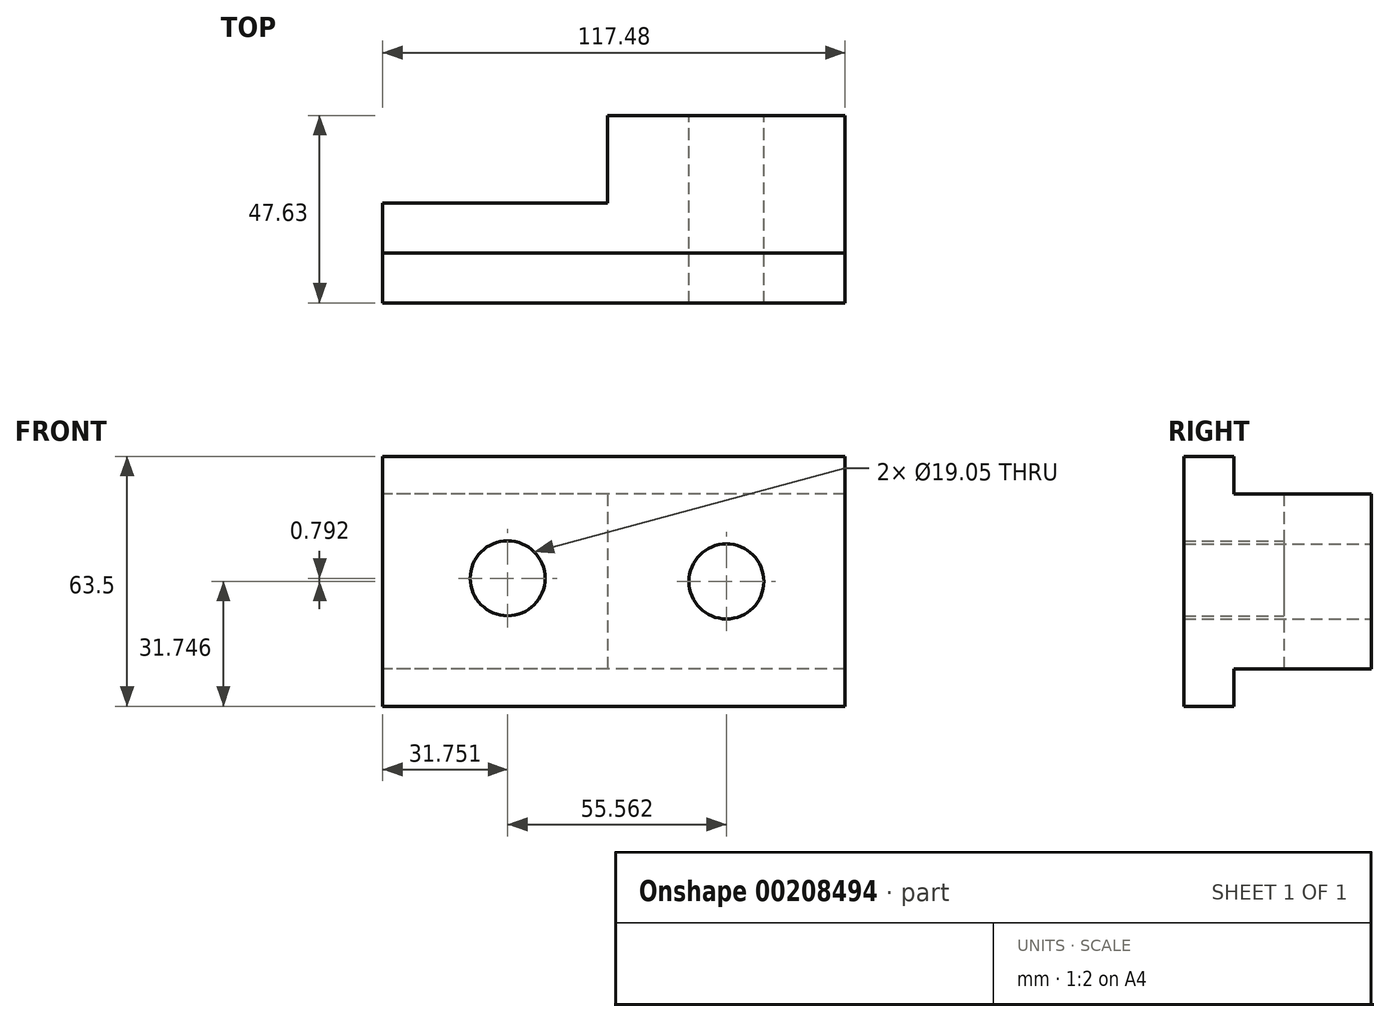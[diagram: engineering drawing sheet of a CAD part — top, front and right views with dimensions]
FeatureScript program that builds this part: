
annotation { "Feature Type Name" : "Feature", "Feature Type Description" : "" }
export const myFeature = defineFeature(function(context is Context, id is Id, definition is map)
    precondition{}
    {
        {
            var Q0;
            Q0=qCreatedBy(makeId("Front.planeOp"),FACE);
            var sketch = newSketch(context, id + "F0", { "sketchPlane" : qUnion([Q0])});
            skLineSegment(sketch, "E0.bottom", {"start": v(30.62, 63.5) * mm, "end": v(148.1, 63.5) * mm});
            skLineSegment(sketch, "E0.top", {"start": v(30.62, 0) * mm, "end": v(148.1, 0) * mm});
            skLineSegment(sketch, "E0.left", {"start": v(30.62, 63.5) * mm, "end": v(30.62, 0) * mm});
            skLineSegment(sketch, "E0.right", {"start": v(148.1, 63.5) * mm, "end": v(148.1, 0) * mm});
            skSolve(sketch);
        }
        {
            var Q0;
            Q0 = qSketchRegion(id + "F0", true);
            extrude(context, id + "F1", {"entities" : qUnion([Q0]), "depth" : 12.7 * mm});
        }
        {
            var Q0;
            Q0=makeQuery(id+"F1.opExtrude","CAP_FACE",FACE,{"disambiguationData":[OSD([sQuery(id+"F0.wireOp",EDGE,"E0.bottom"),sQuery(id+"F0.wireOp",EDGE,"E0.top"),sQuery(id+"F0.wireOp",EDGE,"E0.left"),sQuery(id+"F0.wireOp",EDGE,"E0.right")])],"isStart":true});
            var sketch = newSketch(context, id + "F2", { "sketchPlane" : qUnion([Q0])});
            skLineSegment(sketch, "E1.bottom", {"start": v(-148.1, 53.98) * mm, "end": v(-30.62, 53.98) * mm});
            skLineSegment(sketch, "E1.top", {"start": v(-148.1, 9.53) * mm, "end": v(-30.62, 9.53) * mm});
            skLineSegment(sketch, "E1.left", {"start": v(-148.1, 53.98) * mm, "end": v(-148.1, 9.53) * mm});
            skLineSegment(sketch, "E1.right", {"start": v(-30.62, 53.98) * mm, "end": v(-30.62, 9.53) * mm});
            skSolve(sketch);
        }
        {
            var Q0;
            Q0=makeQuery(id+"F2.imprint","IMPRINT",FACE,{"disambiguationData":[TD([[makeQuery(id+"F2.imprint","IMPRINT",EDGE,{"derivedFrom":sQuery(id+"F2.wireOp",EDGE,"E1.bottom")}),-1.0]])]});
            extrude(context, id + "F3", {"entities" : qUnion([Q0]), "operationType" : NewBodyOperationType.ADD, "depth" : 12.7 * mm});
        }
        {
            var Q0;
            Q0=makeQuery(id+"F3.opExtrude","CAP_FACE",FACE,{"disambiguationData":[OSD([sQuery(id+"F2.wireOp",EDGE,"E1.bottom"),sQuery(id+"F2.wireOp",EDGE,"E1.top"),sQuery(id+"F2.wireOp",EDGE,"E1.left"),sQuery(id+"F2.wireOp",EDGE,"E1.right")])],"isStart":false});
            var sketch = newSketch(context, id + "F4", { "sketchPlane" : qUnion([Q0])});
            skLineSegment(sketch, "E2.bottom", {"start": v(-148.1, 53.98) * mm, "end": v(-87.77, 53.98) * mm});
            skLineSegment(sketch, "E2.top", {"start": v(-148.1, 9.53) * mm, "end": v(-87.77, 9.53) * mm});
            skLineSegment(sketch, "E2.left", {"start": v(-148.1, 53.98) * mm, "end": v(-148.1, 9.53) * mm});
            skLineSegment(sketch, "E2.right", {"start": v(-87.77, 53.98) * mm, "end": v(-87.77, 9.53) * mm});
            skSolve(sketch);
        }
        {
            var Q0;
            Q0 = qSketchRegion(id + "F4", true);
            extrude(context, id + "F5", {"entities" : qUnion([Q0]), "operationType" : NewBodyOperationType.ADD, "depth" : 22.22 * mm});
        }
        {
            var Q0;
            Q0=makeQuery(id+"F3.opExtrude","CAP_FACE",FACE,{"disambiguationData":[OSD([sQuery(id+"F2.wireOp",EDGE,"E1.bottom"),sQuery(id+"F2.wireOp",EDGE,"E1.top"),sQuery(id+"F2.wireOp",EDGE,"E1.left"),sQuery(id+"F2.wireOp",EDGE,"E1.right")])],"isStart":false});
            var sketch = newSketch(context, id + "F6", { "sketchPlane" : qUnion([Q0])});
            skCircle(sketch, "E3", {"center": v(-62.37, 32.55) * mm, "radius": 9.53 * mm});
            skCircle(sketch, "E4", {"center": v(-117.93, 31.76) * mm, "radius": 9.53 * mm});
            skSolve(sketch);
        }
        {
            var Q0;
            Q0 = qSketchRegion(id + "F6", true);
            extrude(context, id + "F7", {"entities" : qUnion([Q0]), "operationType" : NewBodyOperationType.REMOVE, "endBound" : BoundingType.THROUGH_ALL, "oppositeDirection" : true, "depth" : 25.4 * mm});
        }
        {
            var Q0;
            Q0=makeQuery(id+"F7.boolean.opBoolean","COPY",FACE,{"derivedFrom":makeQuery(id+"F7.opExtrude","CAP_FACE",FACE,{"disambiguationData":[OSD([sQuery(id+"F6.wireOp",EDGE,"E4")])],"isStart":true})});
            extrude(context, id + "F8", {"entities" : qUnion([Q0]), "operationType" : NewBodyOperationType.REMOVE, "endBound" : BoundingType.THROUGH_ALL, "oppositeDirection" : true, "depth" : 25.4 * mm});
        }
    });
